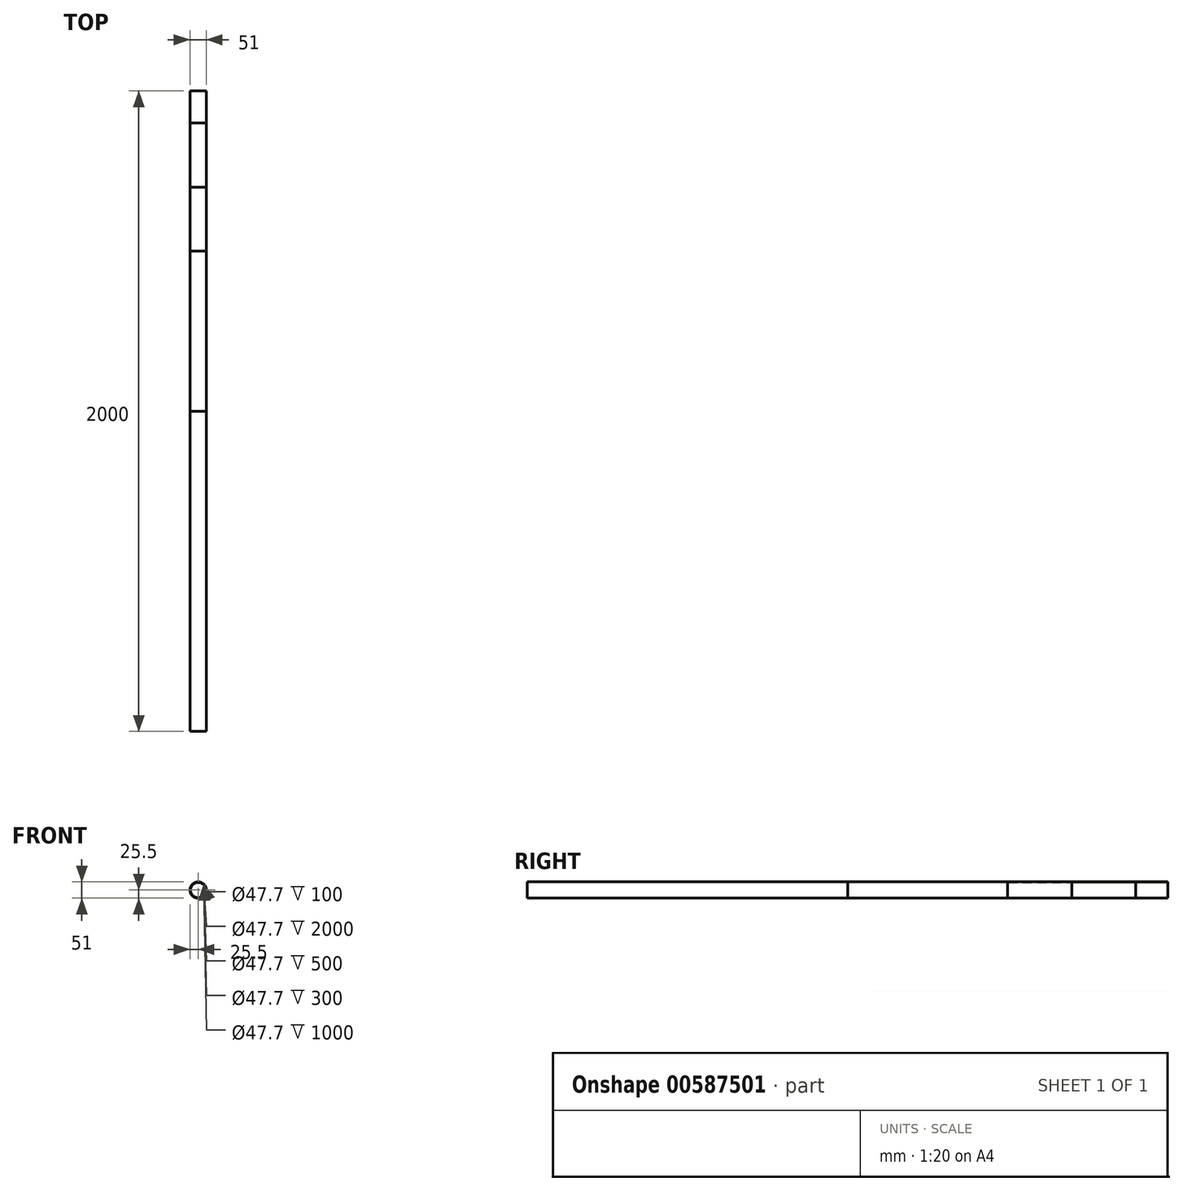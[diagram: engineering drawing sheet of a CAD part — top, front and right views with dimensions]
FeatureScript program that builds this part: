
annotation { "Feature Type Name" : "Feature", "Feature Type Description" : "" }
export const myFeature = defineFeature(function(context is Context, id is Id, definition is map)
    precondition{}
    {
        {
            var Q0;
            Q0=qCreatedBy(makeId("Front.planeOp"),FACE);
            var sketch = newSketch(context, id + "F0", { "sketchPlane" : qUnion([Q0])});
            skCircle(sketch, "E0", {"center": v(0, 0) * mm, "radius": 25.5 * mm});
            skCircle(sketch, "E1.0", {"center": v(0, 0) * mm, "radius": 23.85 * mm});
            skSolve(sketch);
        }
        {
            var Q0;
            Q0=makeQuery(id+"F0.imprint","IMPRINT",FACE,{"disambiguationData":[TD([[makeQuery(id+"F0.imprint","IMPRINT",EDGE,{"derivedFrom":sQuery(id+"F0.wireOp",EDGE,"E0")}),1.0]])]});
            extrude(context, id + "F1", {"entities" : qUnion([Q0]), "depth" : 1000 * mm, "offsetDistance" : 25 * mm});
        }
        {
            var Q0;
            Q0 = qSketchRegion(id + "F0", true);
            extrude(context, id + "F2", {"entities" : qUnion([Q0]), "depth" : 500 * mm, "offsetDistance" : 25 * mm});
        }
        {
            var Q0;
            Q0 = qSketchRegion(id + "F0", true);
            extrude(context, id + "F3", {"entities" : qUnion([Q0]), "depth" : 300 * mm, "offsetDistance" : 25 * mm});
        }
        {
            var Q0;
            Q0 = qSketchRegion(id + "F0", true);
            extrude(context, id + "F4", {"entities" : qUnion([Q0]), "depth" : 100 * mm, "offsetDistance" : 25 * mm});
        }
        {
            var Q0;
            Q0 = qSketchRegion(id + "F0", true);
            extrude(context, id + "F5", {"entities" : qUnion([Q0]), "depth" : 2000 * mm, "offsetDistance" : 25 * mm});
        }
    });
